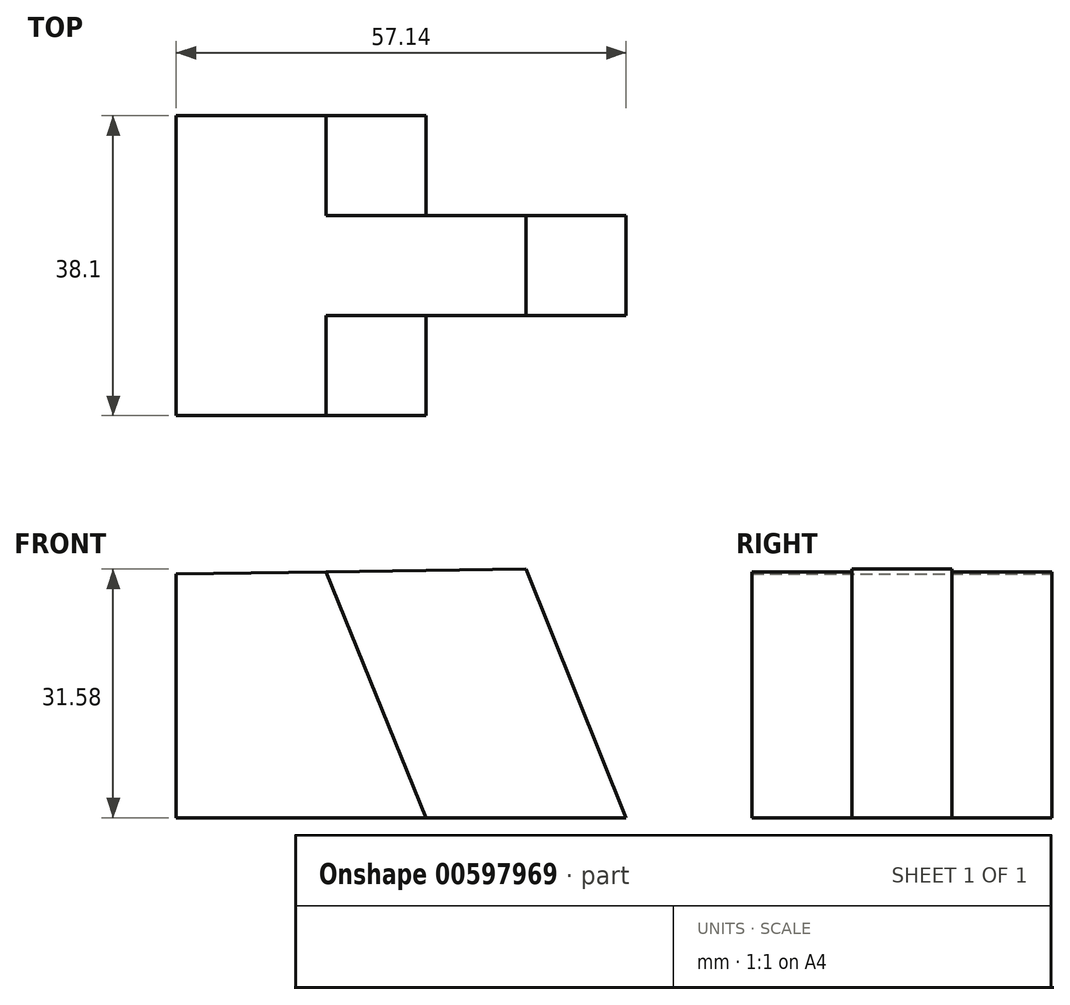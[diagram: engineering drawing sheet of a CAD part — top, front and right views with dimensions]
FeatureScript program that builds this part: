
annotation { "Feature Type Name" : "Feature", "Feature Type Description" : "" }
export const myFeature = defineFeature(function(context is Context, id is Id, definition is map)
    precondition{}
    {
        {
            var Q0;
            Q0=qCreatedBy(makeId("Front.planeOp"),FACE);
            var sketch = newSketch(context, id + "F0", { "sketchPlane" : qUnion([Q0])});
            skLineSegment(sketch, "E0", {"start": v(-64.7, 30.97) * mm, "end": v(-64.7, 0) * mm});
            skLineSegment(sketch, "E1", {"start": v(-64.7, 0) * mm, "end": v(-7.55, 0) * mm});
            skLineSegment(sketch, "E2", {"start": v(-7.55, 0) * mm, "end": v(-7.55, 31.75) * mm});
            skLineSegment(sketch, "E3", {"start": v(-7.55, 31.75) * mm, "end": v(-64.7, 30.97) * mm});
            skSolve(sketch);
        }
        {
            var Q0;
            Q0 = qSketchRegion(id + "F0", true);
            extrude(context, id + "F1", {"entities" : qUnion([Q0]), "depth" : 38.1 * mm, "offsetDistance" : 25.4 * mm});
        }
        {
            var Q0;
            Q0=makeQuery(id+"F1.opExtrude","CAP_FACE",FACE,{"disambiguationData":[OSD([sQuery(id+"F0.wireOp",EDGE,"E0"),sQuery(id+"F0.wireOp",EDGE,"E1"),sQuery(id+"F0.wireOp",EDGE,"E2"),sQuery(id+"F0.wireOp",EDGE,"E3")])],"isStart":false});
            var sketch = newSketch(context, id + "F2", { "sketchPlane" : qUnion([Q0])});
            skLineSegment(sketch, "E4", {"start": v(-45.64, 31.23) * mm, "end": v(-32.94, 0) * mm});
            skSolve(sketch);
        }
        {
            var Q0;
            {var subQ0=sQuery(id+"F2.wireOp",EDGE,"E4");Q0=makeQuery(id+"F2.imprint","IMPRINT",FACE,{"disambiguationData":[TD([[makeQuery(id+"F2.imprint","IMPRINT",EDGE,{"derivedFrom":subQ0}),1.0]])]});}
            extrude(context, id + "F3", {"entities" : qUnion([Q0]), "operationType" : NewBodyOperationType.REMOVE, "oppositeDirection" : true, "depth" : 12.7 * mm, "offsetDistance" : 25.4 * mm});
        }
        {
            var Q0;
            Q0=makeQuery(id+"F1.opExtrude","CAP_FACE",FACE,{"disambiguationData":[OSD([sQuery(id+"F0.wireOp",EDGE,"E0"),sQuery(id+"F0.wireOp",EDGE,"E1"),sQuery(id+"F0.wireOp",EDGE,"E2"),sQuery(id+"F0.wireOp",EDGE,"E3")])],"isStart":true});
            var sketch = newSketch(context, id + "F4", { "sketchPlane" : qUnion([Q0])});
            skLineSegment(sketch, "E5", {"start": v(45.64, 31.23) * mm, "end": v(32.94, 0) * mm});
            skSolve(sketch);
        }
        {
            var Q0;
            Q0 = qSketchRegion(id + "F4", true);
            var Q1;
            {var subQ0=sQuery(id+"F4.wireOp",EDGE,"E5");Q1=makeQuery(id+"F4.imprint","IMPRINT",FACE,{"disambiguationData":[TD([[makeQuery(id+"F4.imprint","IMPRINT",EDGE,{"derivedFrom":subQ0}),-1.0]])]});}
            extrude(context, id + "F5", {"entities" : qUnion([Q0, Q1]), "operationType" : NewBodyOperationType.REMOVE, "oppositeDirection" : true, "depth" : 12.7 * mm, "offsetDistance" : 25.4 * mm});
        }
        {
            var Q0;
            Q0=makeQuery(id+"F5.boolean.opBoolean","COPY",FACE,{"derivedFrom":makeQuery(id+"F5.opExtrude","CAP_FACE",FACE,{"disambiguationData":[OSD([sQuery(id+"F0.wireOp",EDGE,"E1"),sQuery(id+"F0.wireOp",EDGE,"E2"),sQuery(id+"F0.wireOp",EDGE,"E3"),sQuery(id+"F4.wireOp",EDGE,"E5")])],"isStart":false})});
            var sketch = newSketch(context, id + "F6", { "sketchPlane" : qUnion([Q0])});
            skLineSegment(sketch, "E6", {"start": v(20.25, 31.58) * mm, "end": v(7.55, 0) * mm});
            skSolve(sketch);
        }
        {
            var Q0;
            {var subQ0=sQuery(id+"F6.wireOp",EDGE,"E6");Q0=makeQuery(id+"F6.imprint","IMPRINT",FACE,{"disambiguationData":[TD([[makeQuery(id+"F6.imprint","IMPRINT",EDGE,{"derivedFrom":subQ0}),-1.0]])]});}
            extrude(context, id + "F7", {"entities" : qUnion([Q0]), "operationType" : NewBodyOperationType.REMOVE, "endBound" : BoundingType.THROUGH_ALL, "oppositeDirection" : true, "depth" : 25.4 * mm, "offsetDistance" : 25.4 * mm});
        }
    });
